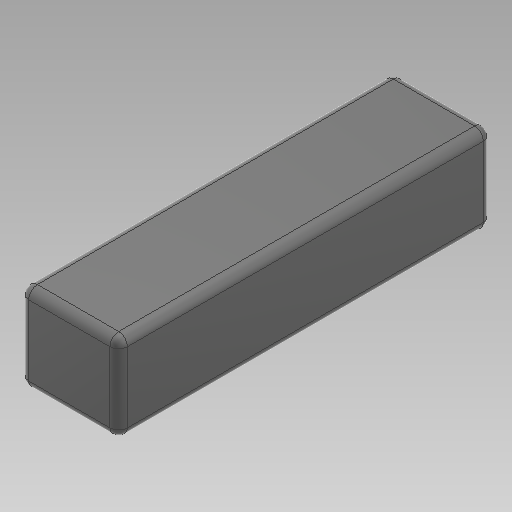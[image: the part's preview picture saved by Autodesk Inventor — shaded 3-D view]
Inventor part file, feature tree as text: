
AUTODESK INVENTOR PART (.ipt)
format: ipt  version: 2020 (Build 240168000, 168)  size: 116,736 bytes
history: native  units: in
note: dims shown in document units (in); Inventor stores cm internally (conversion verified against a paired STEP export)
features: extrude x1, fillet x1, sketch x1
ambient origin geometry x8: Origin, YZ Plane, XZ Plane, XY Plane, X Axis, Y Axis, Z Axis, Center Point
bodies: Solid1 (feature_tree)
feature tree (3):
  extrude  "Extrusion1"  Depth=6.6929in
  fillet  "Fillet1"  Radius=1.5748in
  sketch  "Sketch1"  dims[d0=1.7717in d1=6.6929in d2=1.5748in d3=0.0in d4=0.1575in]
